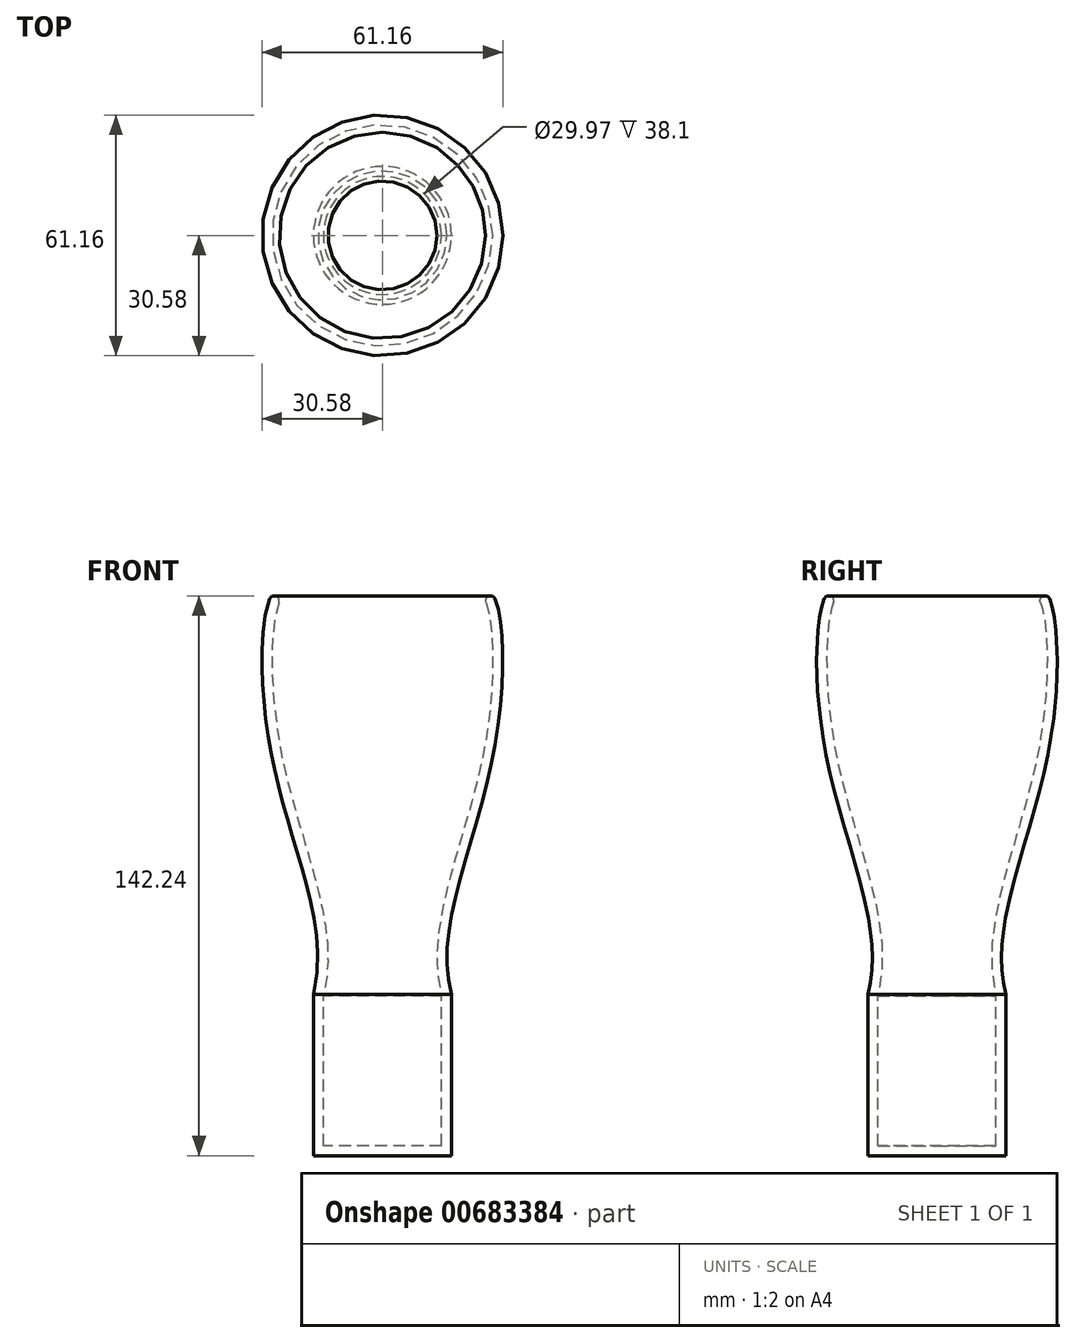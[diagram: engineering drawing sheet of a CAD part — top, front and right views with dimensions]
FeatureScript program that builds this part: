
annotation { "Feature Type Name" : "Feature", "Feature Type Description" : "" }
export const myFeature = defineFeature(function(context is Context, id is Id, definition is map)
    precondition{}
    {
        {
            var Q0;
            Q0=qCreatedBy(makeId("Front.planeOp"),FACE);
            var sketch = newSketch(context, id + "F0", { "sketchPlane" : qUnion([Q0])});
            skLineSegment(sketch, "E0", {"start": v(0, 139.7) * mm, "end": v(0, 0) * mm});
            skLineSegment(sketch, "E1", {"start": v(0, 0) * mm, "end": v(-14.99, 0) * mm});
            skLineSegment(sketch, "E2", {"start": v(-14.99, 0) * mm, "end": v(-14.99, 38.1) * mm});
            skLineSegment(sketch, "E3", {"start": v(0, 139.7) * mm, "end": v(-25.4, 139.7) * mm});
            skFitSpline(sketch, "E4", {"points": [v(-25.4, 139.7) * mm, v(-25.4, 98.3) * mm, v(-14.99, 38.1) * mm], "startDerivative": vector(-22.2, -31.11) * mm, "endDerivative": vector(-25.11, -96.92) * mm});
            skLineSegment(sketch, "E5.MirrorCS", {"start": v(14.99, 0) * mm, "end": v(14.99, 38.1) * mm});
            skFitSpline(sketch, "E6.MirrorCS", {"points": [v(25.4, 139.7) * mm, v(25.4, 98.3) * mm, v(14.99, 38.1) * mm], "startDerivative": vector(22.2, -31.11) * mm, "endDerivative": vector(25.11, -96.92) * mm});
            skFitSpline(sketch, "E7.MirrorCS", {"points": [v(25.4, 139.7) * mm, v(25.4, 98.3) * mm, v(14.99, 38.1) * mm], "startDerivative": vector(22.2, -31.11) * mm, "endDerivative": vector(25.11, -96.92) * mm});
            skLineSegment(sketch, "E8", {"start": v(0, 139.7) * mm, "end": v(25.4, 139.7) * mm});
            skLineSegment(sketch, "E9", {"start": v(0, 0) * mm, "end": v(14.99, 0) * mm});
            skFitSpline(sketch, "E10", {"points": [v(26.62, 105.15) * mm, v(45.57, 101.72) * mm, v(16.57, 65.82) * mm], "startDerivative": vector(82.9, 118.4) * mm, "endDerivative": vector(-43.22, 208.48) * mm});
            skSolve(sketch);
        }
        {
            var Q0;
            Q0=makeQuery(id+"F0.imprint","IMPRINT",FACE,{"disambiguationData":[TD([[makeQuery(id+"F0.imprint","IMPRINT",EDGE,{"derivedFrom":sQuery(id+"F0.wireOp",EDGE,"E0")}),-1.0]])]});
            var Q1;
            Q1=sQuery(id+"F0.wireOp",EDGE,"E0");
            revolve(context, id + "F1", {"entities" : qUnion([Q0]), "axis" : qUnion([Q1]), "revolveType" : RevolveType.FULL});
        }
        {
            var Q0;
            Q0=makeQuery(id+"F1.opRevolve","SWEPT_FACE",FACE,{"disambiguationData":[OSD([sQuery(id+"F0.wireOp",EDGE,"E3")])]});
            shell(context, id + "F2", {"entities" : qUnion([Q0]), "thickness" : 2.54 * mm, "oppositeDirection" : true});
        }
        {
            var Q0;
            Q0=makeQuery(id+"F1.opRevolve","SWEPT_FACE",FACE,{"disambiguationData":[OSD([sQuery(id+"F0.wireOp",EDGE,"E3")])]});
            fillet(context, id + "F3", {"entities" : qUnion([Q0]), "radius" : 1.27 * mm, "tangentPropagation" : true, "allowEdgeOverflow" : false});
        }
    });
